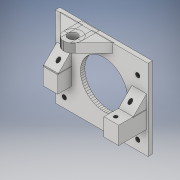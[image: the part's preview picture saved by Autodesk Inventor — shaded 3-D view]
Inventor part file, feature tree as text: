
AUTODESK INVENTOR PART (.ipt)
format: ipt  version: 2017 (Build 210142000, 142)  size: 798,208 bytes
history: native  units: in
note: dims shown in document units (in); Inventor stores cm internally (conversion verified against a paired STEP export)
features: projected_geometry x2, extrude x1, sketch x1, imported_body x1
ambient origin geometry x8: Origin, YZ Plane, XZ Plane, XY Plane, X Axis, Y Axis, Z Axis, Center Point
bodies: Solid1 (feature_tree)
feature tree (5):
  extrude  "Extrusion1"  Depth=0.3937in TaperAngle=0.0deg
  sketch  "Sketch1"  dims[d0=0.252in d1=0.3937in d2=0.0in]
  projected_geometry  "Projected Loop1"
  projected_geometry  "Projected Loop2"
  imported_body  "Base1"
